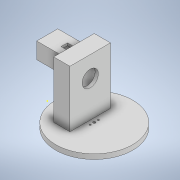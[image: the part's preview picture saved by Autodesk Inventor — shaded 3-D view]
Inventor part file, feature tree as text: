
AUTODESK INVENTOR PART (.ipt)
format: ipt  version: 2022 (Build 260153000, 153)  size: 310,272 bytes
history: native  units: in
note: dims shown in document units (in); Inventor stores cm internally (conversion verified against a paired STEP export)
features: sketch x20, extrude x16, thread x4
ambient origin geometry x8: Origin, YZ Plane, XZ Plane, XY Plane, X Axis, Y Axis, Z Axis, Center Point
bodies: Solid1 (feature_tree)
feature tree (40):
  extrude  "Extrusion1"  Depth=0.2362in TaperAngle=0.0deg
  extrude  "Extrusion2"  Depth=0.7874in
  sketch  "Sketch3"  dims[d5=0.0787in d6=0.9237in d7=0.0in]
  extrude  "Extrusion3"  Depth=0.9237in TaperAngle=0.0deg
  extrude  "Extrusion4"  Depth=0.3937in
  extrude  "Extrusion5"  Depth=1.9685in
  extrude  "Extrusion6"  Depth=2.7559in TaperAngle=0.0deg
  thread  "Thread1"  [1 undecoded]
  thread  "Thread2"  [1 undecoded]
  thread  "Thread3"  [1 undecoded]
  thread  "Thread4"  [1 undecoded]
  extrude  "Extrusion7"  Depth=0.6299in TaperAngle=0.0deg
  extrude  "Extrusion8"  Depth=0.2362in
  extrude  "Extrusion9"  Depth=0.1024in
  extrude  "Extrusion10"  Depth=0.1181in
  extrude  "Extrusion11"  Depth=0.1969in
  sketch  "Sketch13"  dims[d34=0.1063in d35=0.1063in]
  sketch  "Sketch14"  dims[d36=0.3937in d37=0.0in d38=0.3937in d39=0.0in]
  sketch  "Sketch15"  dims[d40=0.3937in d41=0.0in d42=0.3937in d43=0.0in]
  extrude  "Extrusion12"  Depth=0.1063in
  extrude  "Extrusion13"  Depth=0.1063in
  extrude  "Extrusion14"  Depth=0.3937in TaperAngle=0.0deg
  sketch  "Sketch18"  dims[d48=0.6063in d49=0.0in]
  extrude  "Extrusion15"  Depth=0.3937in TaperAngle=0.0deg
  extrude  "Extrusion16"  Depth=0.6693in
  sketch  "Sketch1"  dims[d0=3.7402in d1=0.2362in d2=0.0in]
  sketch  "Sketch2"  dims[d3=0.7874in d4=0.0787in]
  sketch  "Sketch4"  dims[d9=0.3937in d10=0.9843in]
  sketch  "Sketch5"  dims[d11=0.5906in d12=1.9685in]
  sketch  "Sketch6"  dims[d13=0.7874in d14=2.7559in d15=0.0in d16=0.3937in d17=0.7874in d18=0.7874in d19=0.7874in]
  sketch  "Sketch7"  dims[d20=1.5945in d21=0.6299in d22=0.0in]
  sketch  "Sketch8"  dims[d23=0.2362in d24=0.2362in]
  sketch  "Sketch9"  dims[d25=0.2362in d26=0.0in d27=0.1024in]
  sketch  "Sketch10"  dims[d28=0.1181in d29=0.1181in]
  sketch  "Sketch11"  dims[d30=0.1969in d31=0.1969in]
  sketch  "Sketch12"  dims[d32=0.1063in d33=0.1063in]
  sketch  "Sketch16"  dims[d44=0.3937in d45=0.0in d46=0.6693in]
  sketch  "Sketch17"  dims[d47=0.7874in]
  sketch  "Sketch19"  dims[d50=0.1181in]
  sketch  "Sketch20"  dims[d51=0.6063in d52=0.0in d53=0.2047in d54=0.1437in d55=0.0in d56=0.3937in d57=0.0in d58=0.1181in d59=0.2362in d60=0.2362in d61=0.4724in d62=0.0in d63=0.7874in d64=0.1181in d65=0.1181in d66=0.7874in d67=0.1181in d68=1.1811in d69=0.0in d70=0.1181in d71=0.1181in d72=0.1181in d73=0.0in d74=0.1181in d75=0.7874in d76=0.0in d77=0.4724in d78=0.1575in d79=0.1575in d80=0.1575in d81=0.0in d82=0.1181in d83=0.0in]
note: 4 required parameter values undecoded (feature->parameter linkage not recoverable at this tier; creation-order binding heuristic only, values carry confidence <= 0.55)
